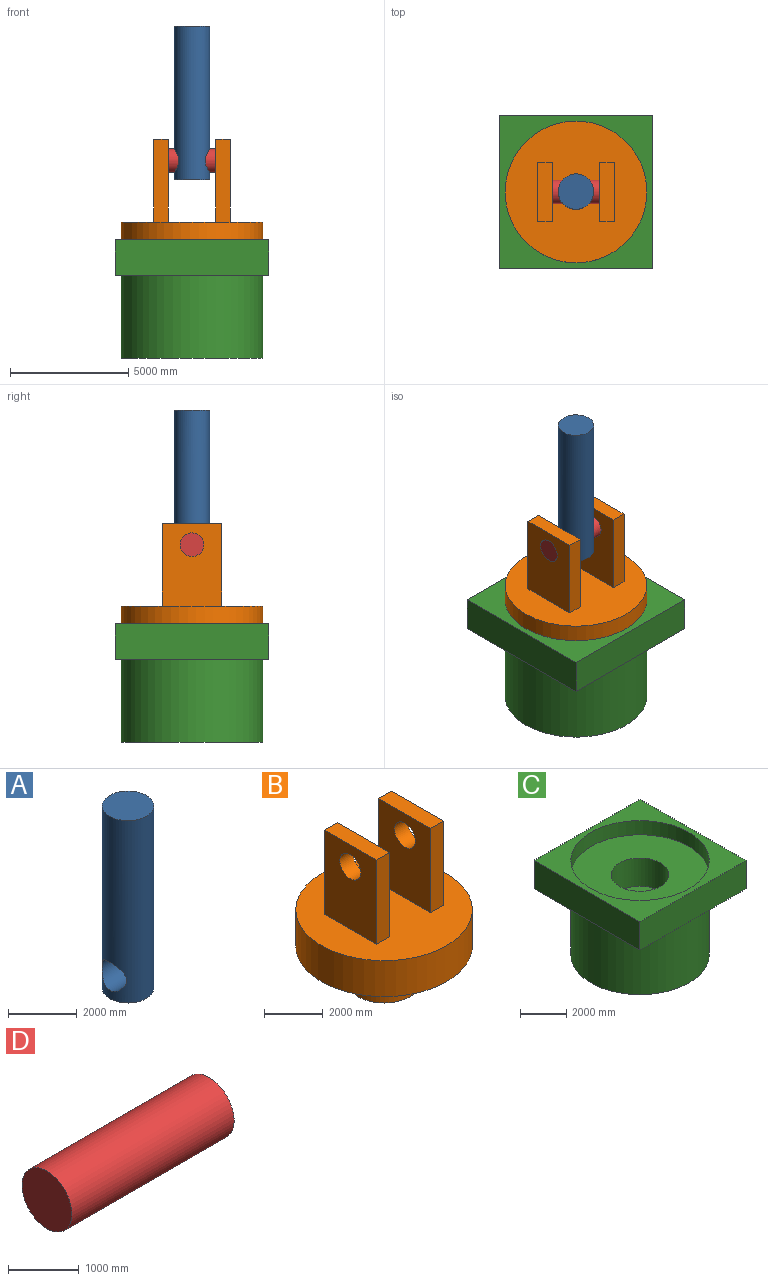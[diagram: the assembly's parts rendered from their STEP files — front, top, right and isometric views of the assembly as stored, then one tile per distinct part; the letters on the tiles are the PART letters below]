
ASSEMBLY  parts=4 mates=3
PART A: 4 faces, bbox 1500x1500x6500 mm
  f0: cylinder r=750mm len=6500mm, axis (0,0,-1), area 28954564.9mm2, adj f1,f2,f3
  f1: plane 1500x1500mm, normal (0,0,1), area 1767145.9mm2, adj f0
  f2: plane 1500x1500mm, normal (0,0,-1), area 1767145.9mm2, adj f0
  f3: cylinder r=500mm len=1500mm, axis (1,0,0), area 4133777.9mm2, adj f0
PART B: 17 faces, bbox 6000x6000x6500 mm
  f0: plane 6000x6000mm, normal (0,0,1), area 25149333.9mm2, adj f1,f3,f4,f5,f6,f8,f9,f10
  f1: cylinder r=3000mm len=6000mm, axis (0,0,-1), area 28274333.9mm2, adj f0,f2
  f2: plane 6000x6000mm, normal (0,0,-1), area 23365595.4mm2, adj f1,f13
  f3: plane 3500x2500mm, normal (-1,0,0), area 7964601.8mm2, adj f0,f4,f6,f7,f16
  f4: plane 3500x625mm, normal (0,-1,0), area 2187500mm2, adj f0,f3,f5,f7
  f5: plane 3500x2500mm, normal (1,0,0), area 7964601.8mm2, adj f0,f4,f6,f7,f16
  f6: plane 3500x625mm, normal (0,1,0), area 2187500mm2, adj f0,f3,f5,f7
  f7: plane 2500x625mm, normal (0,0,1), area 1562500mm2, adj f3,f4,f5,f6
  f8: plane 3500x625mm, normal (0,1,0), area 2187500mm2, adj f0,f9,f11,f12
  f9: plane 3500x2500mm, normal (-1,0,0), area 7964601.8mm2, adj f0,f8,f10,f12,f15
  f10: plane 3500x625mm, normal (0,-1,0), area 2187500mm2, adj f0,f9,f11,f12
  f11: plane 3500x2500mm, normal (1,0,0), area 7964601.8mm2, adj f0,f8,f10,f12,f15
  f12: plane 2500x625mm, normal (0,0,1), area 1562500mm2, adj f8,f9,f10,f11
  f13: cylinder r=1250mm len=2500mm, axis (0,0,1), area 11780972.5mm2, adj f2,f14
  f14: plane 2500x2500mm, normal (0,0,-1), area 4908738.5mm2, adj f13
  f15: cylinder r=500mm len=1000mm, axis (1,0,0), area 1963495.4mm2, adj f9,f11
  f16: cylinder r=500mm len=1000mm, axis (1,0,0), area 1963495.4mm2, adj f3,f5
PART C: 12 faces, bbox 6500x6500x5000 mm
  f0: plane 6500x1500mm, normal (1,0,0), area 9750000mm2, adj f1,f3,f4,f5
  f1: plane 6500x1500mm, normal (0,1,0), area 9750000mm2, adj f0,f2,f4,f5
  f2: plane 6500x1500mm, normal (-1,0,0), area 9750000mm2, adj f1,f3,f4,f5
  f3: plane 6500x1500mm, normal (0,-1,0), area 9750000mm2, adj f0,f2,f4,f5
  f4: plane 6500x6500mm, normal (0,0,1), area 13975666.1mm2, adj f0,f1,f2,f3,f8
  f5: plane 6500x6500mm, normal (0,0,-1), area 13975666.1mm2, adj f0,f1,f2,f3,f6
  f6: cylinder r=3000mm len=6000mm, axis (0,0,1), area 65973445.7mm2, adj f5,f7
  f7: plane 6000x6000mm, normal (0,0,-1), area 28274333.9mm2, adj f6
  f8: cylinder r=3000mm len=6000mm, axis (0,0,-1), area 14137166.9mm2, adj f4,f9
  f9: plane 6000x6000mm, normal (0,0,1), area 23365595.4mm2, adj f8,f10
  f10: cylinder r=1250mm len=2500mm, axis (0,0,1), area 11780972.5mm2, adj f9,f11
  f11: plane 2500x2500mm, normal (0,0,1), area 4908738.5mm2, adj f10
PART D: 3 faces, bbox 3250x1000x1000 mm
  f0: plane 1000x1000mm, normal (-1,0,0), area 785398.2mm2, adj f1
  f1: cylinder r=500mm len=3250mm, axis (1,0,0), area 10210176.1mm2, adj f0,f2
  f2: plane 1000x1000mm, normal (1,0,0), area 785398.2mm2, adj f1
PLACE A t=(-0.04,0,0)mm
PLACE B at identity
PLACE C at identity fixed
PLACE D at identity
MATE revolute D.f1 <-> B.f15  axis (1,0,0) through (1625,0,4850)mm
MATE revolute B.f1 <-> C.f6  axis (0,0,-1) through (0,0,-750)mm
MATE fastened A.f3 <-> D.f1  axis (1,0,0) through (0,0,4850)mm
